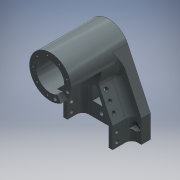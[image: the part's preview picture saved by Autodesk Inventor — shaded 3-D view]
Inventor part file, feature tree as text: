
AUTODESK INVENTOR PART (.ipt)
format: ipt  version: 2016 (Build 200138000, 138)  size: 448,512 bytes
history: native  units: mm
features: extrude x15, sketch x15, fillet x5
ambient origin geometry x8: Origin, YZ Plane, XZ Plane, XY Plane, X Axis, Y Axis, Z Axis, Center Point
bodies: Solid1 (feature_tree)
feature tree (35):
  extrude  "Extrusion1"  Depth=18.0mm
  extrude  "Extrusion2"  Depth=18.0mm
  extrude  "Extrusion5"  Depth=12.5mm
  extrude  "Extrusion8"  Depth=3.2mm
  extrude  "Extrusion9"  Depth=60.0mm TaperAngle=360.0deg
  extrude  "Extrusion11"  Depth=27.5mm
  extrude  "Extrusion12"  Depth=27.5mm
  extrude  "Extrusion13"  Depth=27.5mm
  extrude  "Extrusion14"  Depth=18.0mm
  extrude  "Extrusion15"  Depth=82.5mm
  fillet  "Fillet1"  Radius=6.0mm
  sketch  "Sketch17"  dims[d36=27.0mm d37=0.0mm d59=6.0mm d60=0.0mm]
  fillet  "Fillet2"  Radius=37.0mm
  extrude  "Extrusion17"  Depth=6.0mm TaperAngle=0.0deg
  extrude  "Extrusion18"  Depth=5.0mm
  extrude  "Extrusion19"  Depth=11.625mm
  extrude  "Extrusion20"  Depth=5.0mm
  extrude  "Extrusion22"  Depth=10.0mm TaperAngle=0.0deg
  fillet  "Fillet7"  Radius=6.0mm
  fillet  "Fillet8"  Radius=7.0mm
  fillet  "Fillet9"  Radius=17.5mm
  sketch  "Sketch1"  dims[d7=18.0mm d9=18.0mm d10=18.0mm]
  sketch  "Sketch2"  dims[d11=18.0mm d12=18.0mm]
  sketch  "Sketch5"  dims[d13=82.5mm d14=12.5mm]
  sketch  "Sketch7"  dims[d15=7.0mm d16=3.2mm]
  sketch  "Sketch8"  dims[d17=15.5mm d18=60.0mm d20=360.0deg]
  sketch  "Sketch11"  dims[d22=30.0mm d23=27.5mm]
  sketch  "Sketch13"  dims[d24=18.0mm d25=27.5mm]
  sketch  "Sketch14"  dims[d26=27.5mm d27=27.5mm]
  sketch  "Sketch15"  dims[d29=18.0mm d30=18.0mm]
  sketch  "Sketch16"  dims[d31=82.5mm d32=82.5mm d33=6.0mm d34=0.0mm d35=37.0mm]
  sketch  "Sketch18"  dims[d63=5.0mm d64=5.0mm]
  sketch  "Sketch20"  dims[d65=11.625mm d66=11.625mm]
  sketch  "Sketch21"  dims[d67=9.0mm d73=5.0mm]
  sketch  "Sketch22"  dims[d85=11.625mm d86=10.0mm d87=0.0mm d88=6.0mm d89=7.0mm d90=17.5mm d91=10.0mm d92=0.0mm d97=35.0mm d98=0.0mm d100=30.0deg d101=30.0deg d102=5.0mm d103=5.0mm d104=15.0deg d105=15.0deg d106=37.0mm d107=46.0mm d108=23.0mm d109=9.0mm d110=9.0mm d111=9.0mm d112=0.0mm d113=2.2mm d114=23.0mm d115=90.0mm d117=360.0deg d119=14.0mm d120=0.0mm d121=10.4mm d122=5.0mm d123=0.0mm d124=5.0mm d125=20.0mm d126=0.0mm d127=8.0mm d128=5.0mm d129=5.0mm d130=5.0mm d131=6.0mm d132=6.0mm d133=12.0mm d134=12.0mm d135=5.0mm d136=12.0mm d141=10.9mm d143=0.0mm d144=0.0mm d148=5.0mm d149=5.0mm d150=5.0mm d151=25.0mm d152=0.0mm d155=5.0mm d156=6.0mm d157=6.0mm d158=5.0mm d159=12.0mm d160=0.0mm d161=0.0mm d162=6.0mm d163=6.0mm d164=5.0mm d165=12.0mm d166=5.0mm d167=12.0mm d168=12.0mm d169=0.0mm d172=12.0mm d173=0.0mm d175=8.0mm d176=8.0mm d177=8.0mm]
